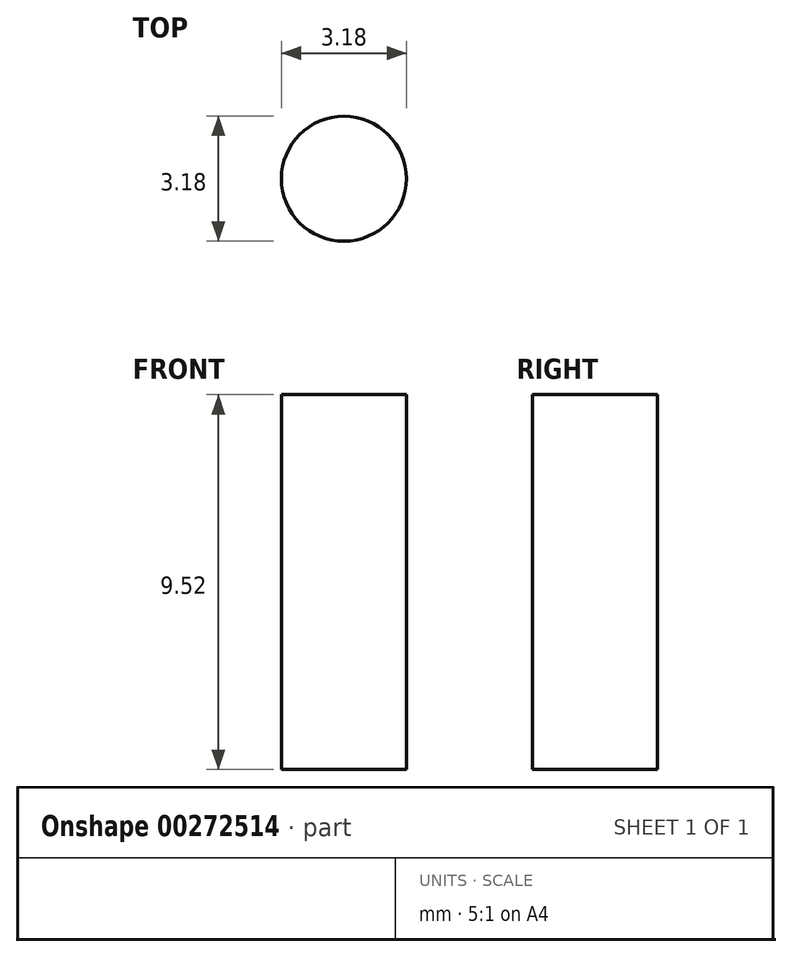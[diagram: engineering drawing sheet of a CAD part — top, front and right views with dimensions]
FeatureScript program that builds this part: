
annotation { "Feature Type Name" : "Feature", "Feature Type Description" : "" }
export const myFeature = defineFeature(function(context is Context, id is Id, definition is map)
    precondition{}
    {
        {
            var Q0;
            Q0=qCreatedBy(makeId("Top.planeOp"),FACE);
            var sketch = newSketch(context, id + "F0", { "sketchPlane" : qUnion([Q0])});
            skCircle(sketch, "E0", {"center": v(0, 0) * mm, "radius": 1.59 * mm});
            skSolve(sketch);
        }
        {
            var Q0;
            Q0=makeQuery(id+"F0.imprint","IMPRINT",FACE,{"disambiguationData":[TD([[makeQuery(id+"F0.imprint","IMPRINT",EDGE,{"derivedFrom":sQuery(id+"F0.wireOp",EDGE,"E0")}),1.0]])]});
            extrude(context, id + "F1", {"entities" : qUnion([Q0]), "depth" : 4.76 * mm, "hasSecondDirection" : true, "secondDirectionOppositeDirection" : true, "secondDirectionDepth" : 4.76 * mm});
        }
    });
